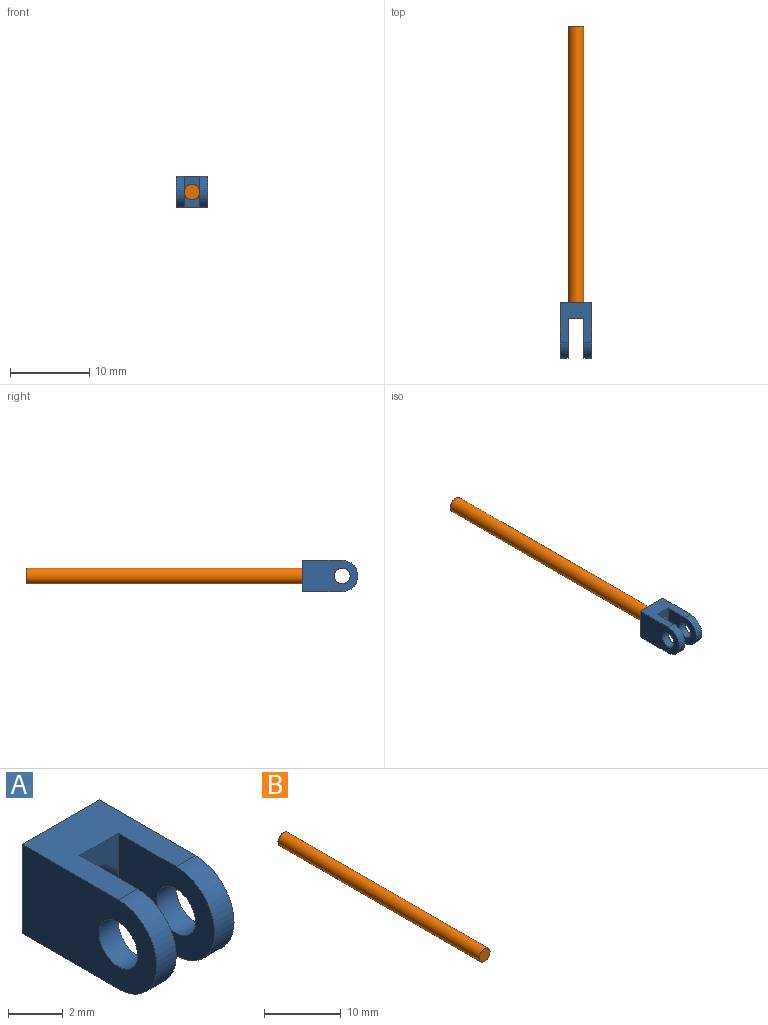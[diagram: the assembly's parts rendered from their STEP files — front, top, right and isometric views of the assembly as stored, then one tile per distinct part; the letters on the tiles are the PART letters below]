
ASSEMBLY  parts=2 mates=1
PART A: 14 faces, bbox 4x7x4 mm
  f0: cylinder r=2mm len=4mm, axis (-1,0,0), area 6.3mm2, adj f2,f3,f9,f11
  f1: cylinder r=1mm len=2mm, axis (1,0,0), area 6.3mm2, adj f9,f11
  f2: plane 5x4mm, normal (0,0,-1), area 14mm2, adj f0,f5,f7,f8,f9,f11,f12,f13
  f3: plane 5x4mm, normal (0,0,1), area 14mm2, adj f0,f5,f7,f8,f9,f10,f11,f12
  f4: cylinder r=1mm len=2mm, axis (0,1,0), area 12.6mm2, adj f7,f10,f13
  f5: cylinder r=2mm len=4mm, axis (-1,0,0), area 6.3mm2, adj f2,f3,f8,f12
  f6: cylinder r=1mm len=2mm, axis (1,0,0), area 6.3mm2, adj f8,f12
  f7: plane 4x4mm, normal (0,1,0), area 12.9mm2, adj f2,f3,f4,f8,f9
  f8: plane 7x4mm, normal (1,0,0), area 23.1mm2, adj f2,f3,f5,f6,f7
  f9: plane 7x4mm, normal (-1,0,0), area 23.1mm2, adj f0,f1,f2,f3,f7
  f10: plane 2x2mm, normal (0,-1,0), area 2.4mm2, adj f3,f4,f11,f12
  f11: plane 5x4mm, normal (1,0,0), area 15.1mm2, adj f0,f1,f2,f3,f10,f13
  f12: plane 5x4mm, normal (-1,0,0), area 15.1mm2, adj f2,f3,f5,f6,f10,f13
  f13: plane 2x2mm, normal (0,-1,0), area 2.4mm2, adj f2,f4,f11,f12
PART B: 3 faces, bbox 2x37x2 mm
  f0: cylinder r=1mm len=37mm, axis (0,1,0), area 232.5mm2, adj f1,f2
  f1: plane 2x2mm, normal (0,-1,0), area 3.1mm2, adj f0
  f2: plane 2x2mm, normal (0,1,0), area 3.1mm2, adj f0
PLACE A t=(4.42,-5.16,5.6)mm
PLACE B t=(6.42,34.84,5.6)mm
MATE fastened B.f0 <-> A.f4  axis (0,-1,0) through (6.42,-2.16,5.6)mm
